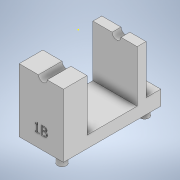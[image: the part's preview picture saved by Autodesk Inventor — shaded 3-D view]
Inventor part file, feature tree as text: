
AUTODESK INVENTOR PART (.ipt)
format: ipt  version: 2021 (Build 250183000, 183)  size: 207,872 bytes
history: native  units: mm
features: sketch x7, extrude x5, emboss x1
ambient origin geometry x8: Origin, YZ Plane, XZ Plane, XY Plane, X Axis, Y Axis, Z Axis, Center Point
bodies: Solid1 (feature_tree)
feature tree (13):
  extrude  "Extrusion1"  Depth=21.477mm
  extrude  "Extrusion2"  Depth=3.0mm
  extrude  "Extrusion3"  Depth=3.0mm
  extrude  "Extrusion4"  Depth=3.0mm
  sketch  "Sketch5"  dims[d9=3.0mm d10=3.0mm d11=0.0mm]
  extrude  "Extrusion5"  Depth=3.0mm TaperAngle=0.0deg
  emboss  "Emboss1"
  sketch  "Sketch1"  dims[d0=33.0mm d1=21.477mm]
  sketch  "Sketch2"  dims[d2=15.0mm d3=0.0mm d4=3.0mm]
  sketch  "Sketch3"  dims[d5=2.5mm d6=3.0mm]
  sketch  "Sketch4"  dims[d7=28.0mm d8=3.0mm]
  sketch  "Sketch6"  dims[d12=8.0mm]
  sketch  "Sketch7"  dims[d13=8.0mm d14=20.0mm d15=0.0mm d16=0.0mm d17=3.0mm d18=6.983mm d19=0.0mm d20=0.0mm d21=5.0mm d22=5.0mm d23=0.0mm d24=1.0mm d25=0.0mm]
